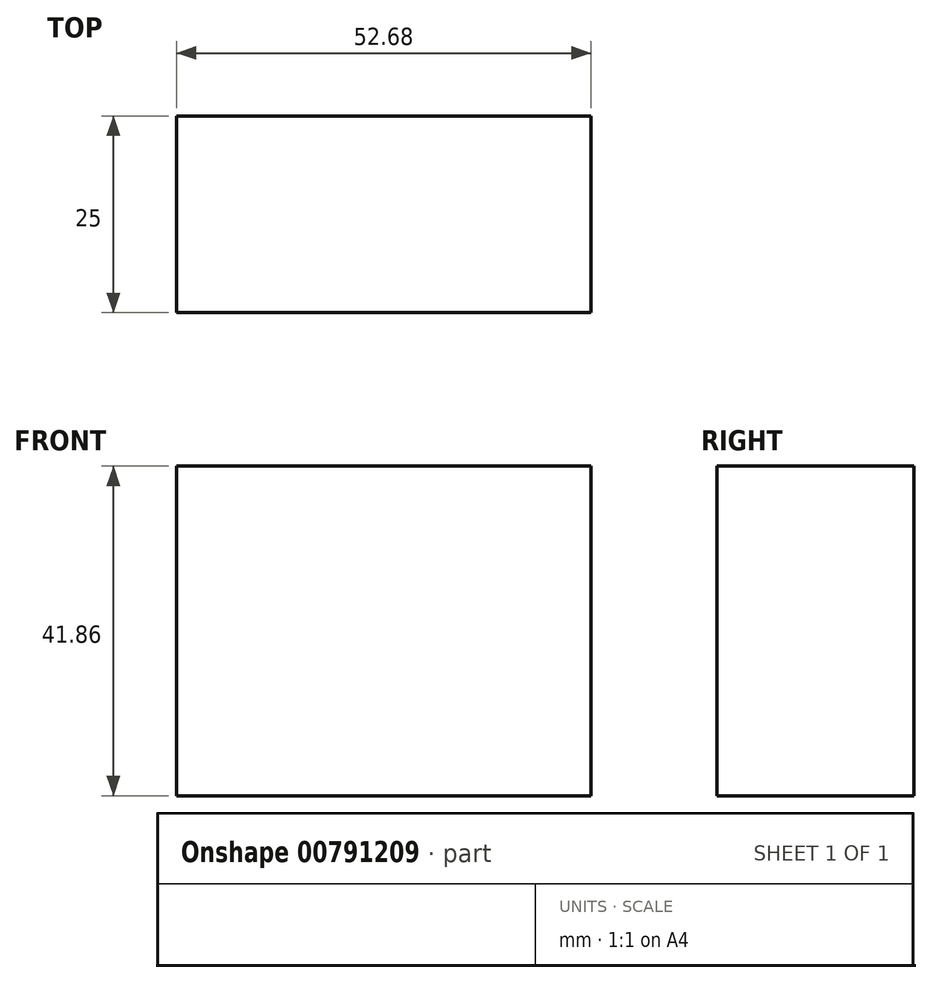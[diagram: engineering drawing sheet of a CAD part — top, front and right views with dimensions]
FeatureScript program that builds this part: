
annotation { "Feature Type Name" : "Feature", "Feature Type Description" : "" }
export const myFeature = defineFeature(function(context is Context, id is Id, definition is map)
    precondition{}
    {
        {
            var Q0;
            Q0=qCreatedBy(makeId("Front.planeOp"),FACE);
            var sketch = newSketch(context, id + "F0", { "sketchPlane" : qUnion([Q0])});
            skLineSegment(sketch, "E0.bottom", {"start": v(16.95, 9.19) * mm, "end": v(69.63, 9.19) * mm});
            skLineSegment(sketch, "E0.top", {"start": v(16.95, -32.67) * mm, "end": v(69.63, -32.67) * mm});
            skLineSegment(sketch, "E0.left", {"start": v(16.95, 9.19) * mm, "end": v(16.95, -32.67) * mm});
            skLineSegment(sketch, "E0.right", {"start": v(69.63, 9.19) * mm, "end": v(69.63, -32.67) * mm});
            skSolve(sketch);
        }
        {
            var Q0;
            Q0 = qSketchRegion(id + "F0", true);
            extrude(context, id + "F1", {"entities" : qUnion([Q0]), "endBound" : BoundingType.SYMMETRIC, "depth" : 25 * mm, "offsetDistance" : 25 * mm});
        }
    });
